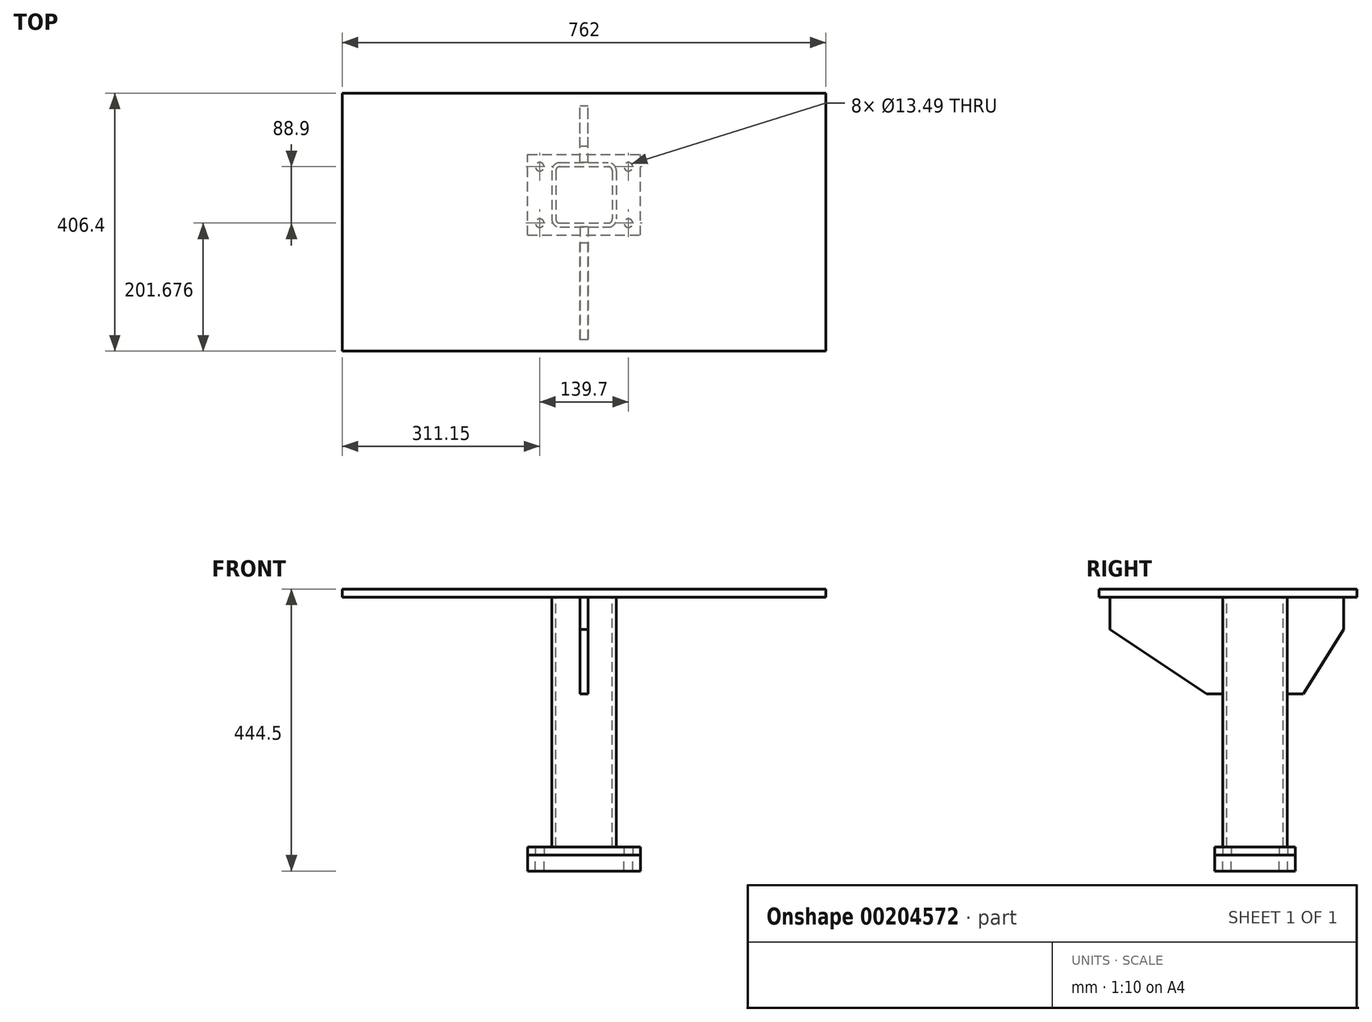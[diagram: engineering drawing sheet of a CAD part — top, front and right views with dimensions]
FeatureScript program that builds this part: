
annotation { "Feature Type Name" : "Feature", "Feature Type Description" : "" }
export const myFeature = defineFeature(function(context is Context, id is Id, definition is map)
    precondition{}
    {
        {
            var Q0;
            Q0=qCreatedBy(makeId("Top.planeOp"),FACE);
            var sketch = newSketch(context, id + "F0", { "sketchPlane" : qUnion([Q0])});
            skLineSegment(sketch, "E0.bottom", {"start": v(-381, 203.2) * mm, "end": v(381, 203.2) * mm});
            skLineSegment(sketch, "E0.top", {"start": v(-381, -203.2) * mm, "end": v(381, -203.2) * mm});
            skLineSegment(sketch, "E0.left", {"start": v(-381, 203.2) * mm, "end": v(-381, -203.2) * mm});
            skLineSegment(sketch, "E0.right", {"start": v(381, 203.2) * mm, "end": v(381, -203.2) * mm});
            skPoint(sketch, "E0.middle", {"position": v(0, 0) * mm});
            skSolve(sketch);
        }
        {
            var Q0;
            Q0 = qSketchRegion(id + "F0", true);
            extrude(context, id + "F1", {"entities" : qUnion([Q0]), "depth" : 12.7 * mm});
        }
        {
            var Q0;
            Q0=makeQuery(id+"F1.opExtrude","CAP_FACE",FACE,{"disambiguationData":[OSD([sQuery(id+"F0.wireOp",EDGE,"E0.bottom"),sQuery(id+"F0.wireOp",EDGE,"E0.top"),sQuery(id+"F0.wireOp",EDGE,"E0.left"),sQuery(id+"F0.wireOp",EDGE,"E0.right")])],"isStart":true});
            var sketch = newSketch(context, id + "F2", { "sketchPlane" : qUnion([Q0])});
            skLineSegment(sketch, "E1.0", {"start": v(-381, 203.2) * mm, "end": v(381, 203.2) * mm, "construction": true});
            skLineSegment(sketch, "E2.0", {"start": v(-381, -42.93) * mm, "end": v(381, -42.93) * mm, "construction": true});
            skLineSegment(sketch, "E3", {"start": v(0, 203.2) * mm, "end": v(0, -115.64) * mm, "construction": true});
            skLineSegment(sketch, "E4.bottom", {"start": v(-38.1, -93.73) * mm, "end": v(38.1, -93.73) * mm});
            skLineSegment(sketch, "E4.top", {"start": v(-38.1, 7.87) * mm, "end": v(38.1, 7.87) * mm});
            skLineSegment(sketch, "E4.left", {"start": v(-50.8, -81.03) * mm, "end": v(-50.8, -4.83) * mm});
            skLineSegment(sketch, "E4.right", {"start": v(50.8, -81.03) * mm, "end": v(50.8, -4.83) * mm});
            skPoint(sketch, "E4.middle", {"position": v(0, -42.93) * mm});
            skPoint(sketch, "E5.visualSharp", {"position": v(-50.8, 7.87) * mm});
            skArc(sketch, "E5.filletArc", {"start": v(-38.1, 7.87) * mm, "mid": v(-47.08, 4.15) * mm, "end": v(-50.8, -4.83) * mm});
            skPoint(sketch, "E6.visualSharp", {"position": v(50.8, 7.87) * mm});
            skArc(sketch, "E6.filletArc", {"start": v(50.8, -4.83) * mm, "mid": v(47.08, 4.15) * mm, "end": v(38.1, 7.87) * mm});
            skPoint(sketch, "E7.visualSharp", {"position": v(50.8, -93.73) * mm});
            skArc(sketch, "E7.filletArc", {"start": v(38.1, -93.73) * mm, "mid": v(47.08, -90) * mm, "end": v(50.8, -81.03) * mm});
            skPoint(sketch, "E8.visualSharp", {"position": v(-50.8, -93.73) * mm});
            skArc(sketch, "E8.filletArc", {"start": v(-50.8, -81.03) * mm, "mid": v(-47.08, -90) * mm, "end": v(-38.1, -93.73) * mm});
            skArc(sketch, "E9.0", {"start": v(-38.1, 1.52) * mm, "mid": v(-42.6, -0.34) * mm, "end": v(-44.45, -4.83) * mm});
            skLineSegment(sketch, "E9.1", {"start": v(-44.45, -81.03) * mm, "end": v(-44.45, -4.83) * mm});
            skLineSegment(sketch, "E9.2", {"start": v(-38.1, 1.52) * mm, "end": v(38.1, 1.52) * mm});
            skArc(sketch, "E9.3", {"start": v(-44.45, -81.03) * mm, "mid": v(-42.6, -85.52) * mm, "end": v(-38.1, -87.38) * mm});
            skArc(sketch, "E9.4", {"start": v(44.45, -4.83) * mm, "mid": v(42.6, -0.34) * mm, "end": v(38.1, 1.52) * mm});
            skLineSegment(sketch, "E9.5", {"start": v(44.45, -81.03) * mm, "end": v(44.45, -4.83) * mm});
            skArc(sketch, "E9.6", {"start": v(38.1, -87.38) * mm, "mid": v(42.6, -85.52) * mm, "end": v(44.45, -81.03) * mm});
            skLineSegment(sketch, "E9.7", {"start": v(-38.1, -87.38) * mm, "end": v(38.1, -87.38) * mm});
            skSolve(sketch);
        }
        {
            var Q0;
            Q0 = qSketchRegion(id + "F2", true);
            extrude(context, id + "F3", {"entities" : qUnion([Q0]), "operationType" : NewBodyOperationType.ADD, "depth" : 393.7 * mm});
        }
        {
            var Q0;
            Q0=makeQuery(id+"F3.opExtrude","CAP_FACE",FACE,{"disambiguationData":[OSD([sQuery(id+"F2.wireOp",EDGE,"E4.bottom"),sQuery(id+"F2.wireOp",EDGE,"E4.top"),sQuery(id+"F2.wireOp",EDGE,"E4.left"),sQuery(id+"F2.wireOp",EDGE,"E4.right"),sQuery(id+"F2.wireOp",EDGE,"E5.filletArc"),sQuery(id+"F2.wireOp",EDGE,"E6.filletArc"),sQuery(id+"F2.wireOp",EDGE,"E7.filletArc"),sQuery(id+"F2.wireOp",EDGE,"E8.filletArc"),sQuery(id+"F2.wireOp",EDGE,"E9.0"),sQuery(id+"F2.wireOp",EDGE,"E9.1"),sQuery(id+"F2.wireOp",EDGE,"E9.2"),sQuery(id+"F2.wireOp",EDGE,"E9.3"),sQuery(id+"F2.wireOp",EDGE,"E9.4"),sQuery(id+"F2.wireOp",EDGE,"E9.5"),sQuery(id+"F2.wireOp",EDGE,"E9.6"),sQuery(id+"F2.wireOp",EDGE,"E9.7")])],"isStart":false});
            var sketch = newSketch(context, id + "F4", { "sketchPlane" : qUnion([Q0])});
            skArc(sketch, "E10.0.0", {"start": v(-50.8, -81.03) * mm, "mid": v(-47.08, -90) * mm, "end": v(-38.1, -93.73) * mm, "construction": true});
            skLineSegment(sketch, "E10.0.1", {"start": v(-38.1, -93.73) * mm, "end": v(38.1, -93.73) * mm, "construction": true});
            skArc(sketch, "E10.0.2", {"start": v(38.1, -93.73) * mm, "mid": v(47.08, -90) * mm, "end": v(50.8, -81.03) * mm, "construction": true});
            skLineSegment(sketch, "E10.0.3", {"start": v(50.8, -81.03) * mm, "end": v(50.8, -4.83) * mm, "construction": true});
            skArc(sketch, "E10.0.4", {"start": v(50.8, -4.83) * mm, "mid": v(47.08, 4.15) * mm, "end": v(38.1, 7.87) * mm, "construction": true});
            skLineSegment(sketch, "E10.0.5", {"start": v(38.1, 7.87) * mm, "end": v(-38.1, 7.87) * mm, "construction": true});
            skArc(sketch, "E10.0.6", {"start": v(-38.1, 7.87) * mm, "mid": v(-47.08, 4.15) * mm, "end": v(-50.8, -4.83) * mm, "construction": true});
            skLineSegment(sketch, "E10.0.7", {"start": v(-50.8, -4.83) * mm, "end": v(-50.8, -81.03) * mm, "construction": true});
            skLineSegment(sketch, "E11", {"start": v(-50.8, -42.93) * mm, "end": v(50.8, -42.93) * mm, "construction": true});
            skLineSegment(sketch, "E12.bottom", {"start": v(-88.9, 20.57) * mm, "end": v(88.9, 20.57) * mm});
            skLineSegment(sketch, "E12.top", {"start": v(-88.9, -106.43) * mm, "end": v(88.9, -106.43) * mm});
            skLineSegment(sketch, "E12.left", {"start": v(-88.9, 20.57) * mm, "end": v(-88.9, -106.43) * mm});
            skLineSegment(sketch, "E12.right", {"start": v(88.9, 20.57) * mm, "end": v(88.9, -106.43) * mm});
            skPoint(sketch, "E12.middle", {"position": v(0, -42.93) * mm});
            skSolve(sketch);
        }
        {
            var Q0;
            Q0=makeQuery(id+"F4.imprint","IMPRINT",FACE,{"disambiguationData":[TD([[makeQuery(id+"F4.imprint","IMPRINT",EDGE,{"derivedFrom":sQuery(id+"F4.wireOp",EDGE,"E12.bottom")}),-1.0]])]});
            var Q1;
            Q1=makeQuery(id+"F4.imprint","IMPRINT",FACE,{"disambiguationData":[TD([[makeQuery(id+"F4.imprint","IMPRINT",EDGE,{"derivedFrom":makeQuery(id+"F3.opExtrude","CAP_EDGE",EDGE,{"disambiguationData":[OSD([sQuery(id+"F2.wireOp",EDGE,"E4.bottom")])],"isStart":false})}),1.0]])]});
            var Q2;
            Q2=makeQuery(id+"F4.imprint","IMPRINT",FACE,{"disambiguationData":[TD([[makeQuery(id+"F4.imprint","IMPRINT",EDGE,{"derivedFrom":makeQuery(id+"F3.opExtrude","CAP_EDGE",EDGE,{"disambiguationData":[OSD([sQuery(id+"F2.wireOp",EDGE,"E9.0")])],"isStart":false})}),1.0]])]});
            extrude(context, id + "F5", {"entities" : qUnion([Q0, Q1, Q2]), "operationType" : NewBodyOperationType.ADD, "depth" : 12.7 * mm});
        }
        {
            var Q0;
            Q0=makeQuery(id+"F5.opExtrude","CAP_FACE",FACE,{"disambiguationData":[OSD([sQuery(id+"F4.wireOp",EDGE,"E12.bottom"),sQuery(id+"F4.wireOp",EDGE,"E12.top"),sQuery(id+"F4.wireOp",EDGE,"E12.left"),sQuery(id+"F4.wireOp",EDGE,"E12.right")])],"isStart":false});
            var sketch = newSketch(context, id + "F6", { "sketchPlane" : qUnion([Q0])});
            skLineSegment(sketch, "E13.0", {"start": v(-88.9, 20.57) * mm, "end": v(-88.9, -106.43) * mm, "construction": true});
            skLineSegment(sketch, "E14.0", {"start": v(88.9, 20.57) * mm, "end": v(88.9, -106.43) * mm, "construction": true});
            skLineSegment(sketch, "E15.0", {"start": v(-69.85, 20.57) * mm, "end": v(-69.85, -106.43) * mm, "construction": true});
            skLineSegment(sketch, "E16", {"start": v(0, 49.65) * mm, "end": v(0, -127.46) * mm, "construction": true});
            skPoint(sketch, "E16.endSnap0", {"position": v(0, -106.43) * mm});
            skLineSegment(sketch, "E17", {"start": v(-88.9, -42.93) * mm, "end": v(-32.15, -42.93) * mm, "construction": true});
            skLineSegment(sketch, "E18.0", {"start": v(-88.9, -87.38) * mm, "end": v(-32.15, -87.38) * mm, "construction": true});
            skPoint(sketch, "E19", {"position": v(-69.85, -87.38) * mm});
            skPoint(sketch, "E20.MirrorP", {"position": v(-69.85, 1.52) * mm});
            skPoint(sketch, "E21.MirrorP", {"position": v(69.85, 1.52) * mm});
            skPoint(sketch, "E22.MirrorP", {"position": v(69.85, -87.38) * mm});
            skSolve(sketch);
        }
        {
            var Q0;
            Q0=sQuery(id+"F6.wireOp",VERTEX,"E20.MirrorP");
            var Q1;
            Q1=sQuery(id+"F6.wireOp",VERTEX,"E19");
            var Q2;
            Q2=sQuery(id+"F6.wireOp",VERTEX,"E22.MirrorP");
            var Q3;
            Q3=sQuery(id+"F6.wireOp",VERTEX,"E21.MirrorP");
            var Q4;
            Q4=makeQuery(id+"F1.opExtrude","SWEPT_BODY",BODY,{"disambiguationData":[OSD([sQuery(id+"F0.wireOp",EDGE,"E0.bottom"),sQuery(id+"F0.wireOp",EDGE,"E0.top"),sQuery(id+"F0.wireOp",EDGE,"E0.left"),sQuery(id+"F0.wireOp",EDGE,"E0.right")])]});
            hole(context, id + "F7", {"style" : HoleStyle.SIMPLE, "endStyle" : HoleEndStyle.BLIND, "standardTappedOrClearance" : lookupTablePath({ "standard" : "ANSI", "fit" : "Normal (ASME)", "size" : "1/2", "type" : "Clearance" }), "standardBlindInLast" : lookupTablePath({ "fit" : "Free", "standard" : "ANSI", "size" : "1/2", "type" : "Clearance" }), "holeDiameter" : 13.5 * mm, "holeDepth" : 12.7 * mm, "locations" : qUnion([Q0, Q1, Q2, Q3]), "scope" : qUnion([Q4])});
        }
        {
            var Q0;
            Q0=qCreatedBy(makeId("Right.planeOp"),FACE);
            var sketch = newSketch(context, id + "F8", { "sketchPlane" : qUnion([Q0])});
            skLineSegment(sketch, "E23.0", {"start": v(203.2, 0) * mm, "end": v(-203.2, 0) * mm, "construction": true});
            skLineSegment(sketch, "E24.0", {"start": v(-7.87, -393.7) * mm, "end": v(-7.87, 0) * mm, "construction": true});
            skLineSegment(sketch, "E25.0", {"start": v(93.73, -393.7) * mm, "end": v(93.73, 0) * mm, "construction": true});
            skLineSegment(sketch, "E26.bottom", {"start": v(-7.87, 0) * mm, "end": v(-185.67, 0) * mm});
            skLineSegment(sketch, "E26.top", {"start": v(-7.87, -152.4) * mm, "end": v(-33.27, -152.4) * mm});
            skLineSegment(sketch, "E26.left", {"start": v(-7.87, 0) * mm, "end": v(-7.87, -152.4) * mm});
            skLineSegment(sketch, "E26.right", {"start": v(-185.67, 0) * mm, "end": v(-185.67, -50.8) * mm});
            skLineSegment(sketch, "E27.bottom", {"start": v(93.73, 0) * mm, "end": v(182.63, 0) * mm});
            skLineSegment(sketch, "E27.top", {"start": v(93.73, -152.4) * mm, "end": v(119.13, -152.4) * mm});
            skLineSegment(sketch, "E27.left", {"start": v(93.73, 0) * mm, "end": v(93.73, -152.4) * mm});
            skLineSegment(sketch, "E27.right", {"start": v(182.63, 0) * mm, "end": v(182.63, -50.8) * mm});
            skLineSegment(sketch, "E28.0", {"start": v(203.2, -50.8) * mm, "end": v(-203.2, -50.8) * mm, "construction": true});
            skLineSegment(sketch, "E29.0", {"start": v(-33.27, -368.3) * mm, "end": v(-33.27, 0) * mm, "construction": true});
            skLineSegment(sketch, "E30.0", {"start": v(119.13, -368.3) * mm, "end": v(119.13, 0) * mm, "construction": true});
            skLineSegment(sketch, "E31", {"start": v(-185.67, -50.8) * mm, "end": v(-33.27, -152.4) * mm});
            skLineSegment(sketch, "E32", {"start": v(119.13, -152.4) * mm, "end": v(182.63, -50.8) * mm});
            skPoint(sketch, "E33.orphan", {"position": v(-185.67, -152.4) * mm});
            skPoint(sketch, "E34.orphan", {"position": v(182.63, -152.4) * mm});
            skSolve(sketch);
        }
        {
            var Q0;
            Q0 = qSketchRegion(id + "F8", true);
            extrude(context, id + "F9", {"entities" : qUnion([Q0]), "operationType" : NewBodyOperationType.ADD, "endBound" : BoundingType.SYMMETRIC, "depth" : 12.7 * mm});
        }
        {
            var Q0;
            Q0=makeQuery(id+"F5.opExtrude","CAP_FACE",FACE,{"disambiguationData":[OSD([sQuery(id+"F4.wireOp",EDGE,"E12.bottom"),sQuery(id+"F4.wireOp",EDGE,"E12.top"),sQuery(id+"F4.wireOp",EDGE,"E12.left"),sQuery(id+"F4.wireOp",EDGE,"E12.right")])],"isStart":false});
            var sketch = newSketch(context, id + "F10", { "sketchPlane" : qUnion([Q0])});
            skLineSegment(sketch, "E35.0.0", {"start": v(88.9, 20.57) * mm, "end": v(-88.9, 20.57) * mm});
            skLineSegment(sketch, "E35.0.1", {"start": v(-88.9, 20.57) * mm, "end": v(-88.9, -106.43) * mm});
            skLineSegment(sketch, "E35.0.2", {"start": v(-88.9, -106.43) * mm, "end": v(88.9, -106.43) * mm});
            skLineSegment(sketch, "E35.0.3", {"start": v(88.9, -106.43) * mm, "end": v(88.9, 20.57) * mm});
            skLineSegment(sketch, "E36.0.0", {"start": v(88.9, 20.57) * mm, "end": v(-88.9, 20.57) * mm, "construction": true});
            skLineSegment(sketch, "E36.0.1", {"start": v(-88.9, 20.57) * mm, "end": v(-88.9, -106.43) * mm, "construction": true});
            skLineSegment(sketch, "E36.0.2", {"start": v(-88.9, -106.43) * mm, "end": v(88.9, -106.43) * mm, "construction": true});
            skLineSegment(sketch, "E36.0.3", {"start": v(88.9, -106.43) * mm, "end": v(88.9, 20.57) * mm, "construction": true});
            skCircle(sketch, "E37.0", {"center": v(69.85, -87.38) * mm, "radius": 6.75 * mm});
            skCircle(sketch, "E38.0", {"center": v(69.85, 1.52) * mm, "radius": 6.75 * mm});
            skCircle(sketch, "E39.0", {"center": v(-69.85, -87.38) * mm, "radius": 6.75 * mm});
            skCircle(sketch, "E40.0", {"center": v(-69.85, 1.52) * mm, "radius": 6.75 * mm});
            skSolve(sketch);
        }
        {
            var Q0;
            Q0 = qSketchRegion(id + "F10", true);
            extrude(context, id + "F11", {"entities" : qUnion([Q0]), "depth" : 25.4 * mm});
        }
    });
